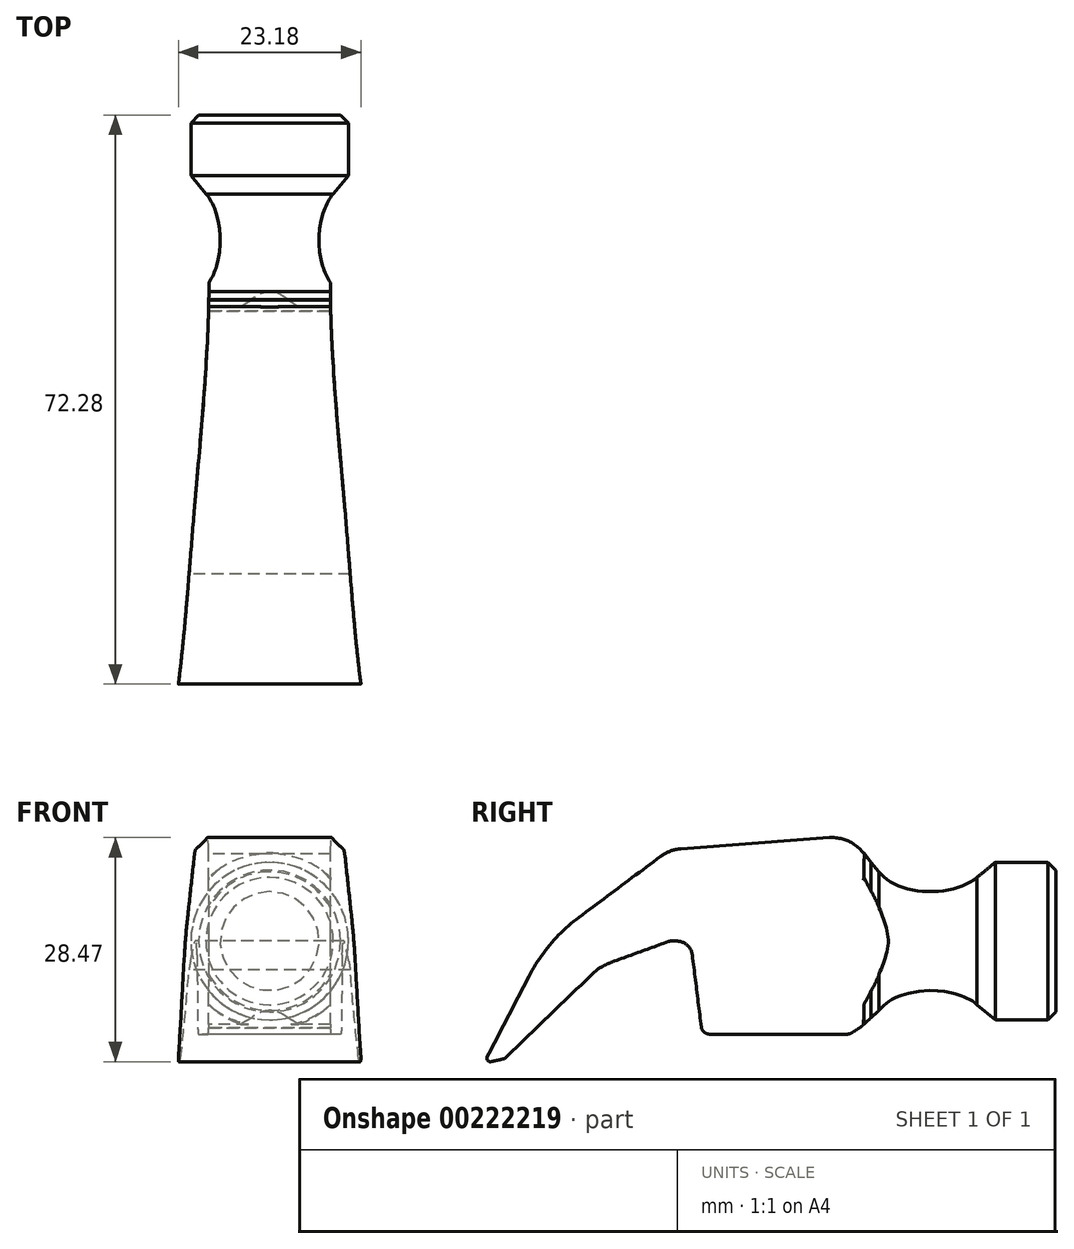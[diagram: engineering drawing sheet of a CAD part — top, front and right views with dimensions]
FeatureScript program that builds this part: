
annotation { "Feature Type Name" : "Feature", "Feature Type Description" : "" }
export const myFeature = defineFeature(function(context is Context, id is Id, definition is map)
    precondition{}
    {
        {
            var Q0;
            Q0=qCreatedBy(makeId("Front.planeOp"),FACE);
            var sketch = newSketch(context, id + "F0", { "sketchPlane" : qUnion([Q0])});
            skCircle(sketch, "E0", {"center": v(0, 0) * mm, "radius": 10 * mm});
            skSolve(sketch);
        }
        {
            var Q0;
            Q0=makeQuery(id+"F0.imprint","IMPRINT",FACE,{"disambiguationData":[TD([[makeQuery(id+"F0.imprint","IMPRINT",EDGE,{"derivedFrom":sQuery(id+"F0.wireOp",EDGE,"E0")}),1.0]])]});
            extrude(context, id + "F1", {"entities" : qUnion([Q0]), "depth" : 25 * mm});
        }
        {
            var Q0;
            Q0=qCreatedBy(makeId("Right.planeOp"),FACE);
            var sketch = newSketch(context, id + "F2", { "sketchPlane" : qUnion([Q0])});
            skEllipse(sketch, "E1", {"center": v(-15.9, 10.31) * mm, "majorRadius": 7.06 * mm, "minorRadius": 4.03 * mm, "majorAxis": v(1, 0)});
            skLineSegment(sketch, "E2", {"start": v(-7.3, 10.31) * mm, "end": v(-10, 8.09) * mm});
            skPoint(sketch, "E2.startSnap0", {"position": v(-8.84, 10.31) * mm});
            skLineSegment(sketch, "E3", {"start": v(-7.3, 10.31) * mm, "end": v(-8.84, 10.31) * mm});
            skSolve(sketch);
        }
        {
            var Q0;
            Q0=makeQuery(id+"F1.opExtrude","CAP_EDGE",EDGE,{"disambiguationData":[OSD([sQuery(id+"F0.wireOp",EDGE,"E0")])],"isStart":false});
            chamfer(context, id + "F3", {"entities" : qUnion([Q0]), "width" : 1 * mm, "tangentPropagation" : true});
        }
        {
            var Q0;
            Q0=makeQuery(id+"F1.opExtrude","CAP_EDGE",EDGE,{"disambiguationData":[OSD([sQuery(id+"F0.wireOp",EDGE,"E0")])],"isStart":true});
            chamfer(context, id + "F4", {"entities" : qUnion([Q0]), "width" : 1 * mm, "tangentPropagation" : true});
        }
        {
            var Q0;
            Q0 = qSketchRegion(id + "F2", true);
            var Q1;
            Q1=makeQuery(id+"F1.opExtrude","SWEPT_FACE",FACE,{"disambiguationData":[OSD([sQuery(id+"F0.wireOp",EDGE,"E0")])]});
            revolve(context, id + "F5", {"operationType" : NewBodyOperationType.REMOVE, "entities" : qUnion([Q0]), "axis" : qUnion([Q1]), "revolveType" : RevolveType.FULL, "oppositeDirection" : true});
        }
        {
            var Q0;
            Q0=qCreatedBy(makeId("Right.planeOp"),FACE);
            var sketch = newSketch(context, id + "F6", { "sketchPlane" : qUnion([Q0])});
            skLineSegment(sketch, "E4", {"start": v(-24.33, 11.06) * mm, "end": v(-24.54, 11.32) * mm});
            skLineSegment(sketch, "E5", {"start": v(-28.78, 13.14) * mm, "end": v(-47.6, 11.73) * mm});
            skLineSegment(sketch, "E6", {"start": v(-50.22, 10.75) * mm, "end": v(-60.56, 3.02) * mm});
            skLineSegment(sketch, "E7", {"start": v(-66.93, -4.48) * mm, "end": v(-72.23, -14.7) * mm});
            skLineSegment(sketch, "E8", {"start": v(-71.76, -15.32) * mm, "end": v(-70.06, -14.95) * mm});
            skLineSegment(sketch, "E9", {"start": v(-70.06, -14.95) * mm, "end": v(-58.3, -3.63) * mm});
            skLineSegment(sketch, "E10", {"start": v(-56.06, -2.55) * mm, "end": v(-49.22, -0.06) * mm});
            skLineSegment(sketch, "E11", {"start": v(-48.88, 0) * mm, "end": v(-48.16, 0) * mm});
            skLineSegment(sketch, "E12", {"start": v(-46.18, -1.75) * mm, "end": v(-45.03, -10.95) * mm});
            skLineSegment(sketch, "E13", {"start": v(-44.04, -11.82) * mm, "end": v(-26.48, -11.82) * mm});
            skLineSegment(sketch, "E14", {"start": v(-25.94, -11.66) * mm, "end": v(-24.86, -10.97) * mm});
            skLineSegment(sketch, "E15", {"start": v(-24.86, -10.97) * mm, "end": v(-24.33, 11.06) * mm});
            skPoint(sketch, "E16.visualSharp", {"position": v(-26.19, 13.33) * mm});
            skArc(sketch, "E16.filletArc", {"start": v(-24.54, 11.32) * mm, "mid": v(-26.44, 12.75) * mm, "end": v(-28.78, 13.14) * mm});
            skPoint(sketch, "E17.visualSharp", {"position": v(-49.05, 11.62) * mm});
            skArc(sketch, "E17.filletArc", {"start": v(-47.6, 11.73) * mm, "mid": v(-48.98, 11.42) * mm, "end": v(-50.22, 10.75) * mm});
            skPoint(sketch, "E18.visualSharp", {"position": v(-64.6, 0) * mm});
            skArc(sketch, "E18.filletArc", {"start": v(-60.56, 3.02) * mm, "mid": v(-64.17, -0.37) * mm, "end": v(-66.93, -4.48) * mm});
            skPoint(sketch, "E19.visualSharp", {"position": v(-44.92, -11.82) * mm});
            skArc(sketch, "E19.filletArc", {"start": v(-45.03, -10.95) * mm, "mid": v(-44.7, -11.57) * mm, "end": v(-44.04, -11.82) * mm});
            skPoint(sketch, "E20.visualSharp", {"position": v(-26.19, -11.82) * mm});
            skArc(sketch, "E20.filletArc", {"start": v(-26.48, -11.82) * mm, "mid": v(-26.2, -11.78) * mm, "end": v(-25.94, -11.66) * mm});
            skPoint(sketch, "E21.visualSharp", {"position": v(-46.4, 0) * mm});
            skArc(sketch, "E21.filletArc", {"start": v(-46.18, -1.75) * mm, "mid": v(-46.84, -0.5) * mm, "end": v(-48.16, 0) * mm});
            skPoint(sketch, "E22.visualSharp", {"position": v(-49.05, 0) * mm});
            skArc(sketch, "E22.filletArc", {"start": v(-48.88, 0) * mm, "mid": v(-49.05, -0.02) * mm, "end": v(-49.22, -0.06) * mm});
            skPoint(sketch, "E23.visualSharp", {"position": v(-57.84, -3.2) * mm});
            skPoint(sketch, "E24.visualSharp", {"position": v(-72.65, -15.5) * mm});
            skArc(sketch, "E24.filletArc", {"start": v(-72.23, -14.7) * mm, "mid": v(-72.2, -15.16) * mm, "end": v(-71.76, -15.32) * mm});
            skPoint(sketch, "E25.visualSharp", {"position": v(-70.06, -14.95) * mm});
            skArc(sketch, "E25.filletArc", {"start": v(-70.06, -14.95) * mm, "mid": v(-70.06, -14.95) * mm, "end": v(-70.06, -14.95) * mm});
            skPoint(sketch, "E26", {"position": v(-57.3, -4.06) * mm});
            skPoint(sketch, "E27", {"position": v(-57.23, -4.15) * mm});
            skPoint(sketch, "E28", {"position": v(-57.49, -3.07) * mm});
            skPoint(sketch, "E29", {"position": v(-58.09, -3.43) * mm});
            skPoint(sketch, "E30", {"position": v(-57.64, -3.12) * mm});
            skPoint(sketch, "E31", {"position": v(-58, -3.34) * mm});
            skLineSegment(sketch, "E32", {"start": v(-58.22, -3.59) * mm, "end": v(-58.3, -3.63) * mm});
            skPoint(sketch, "E33.visualSharp", {"position": v(-57.2, -2.96) * mm});
            skArc(sketch, "E33.filletArc", {"start": v(-56.06, -2.55) * mm, "mid": v(-57.17, -3.01) * mm, "end": v(-58.22, -3.59) * mm});
            skSolve(sketch);
        }
        {
            var Q0;
            Q0=makeQuery(id+"F6.imprint","IMPRINT",FACE,{"disambiguationData":[TD([[makeQuery(id+"F6.imprint","IMPRINT",EDGE,{"derivedFrom":sQuery(id+"F6.wireOp",EDGE,"E4")}),1.0]])]});
            extrude(context, id + "F7", {"entities" : qUnion([Q0]), "operationType" : NewBodyOperationType.ADD, "endBound" : BoundingType.SYMMETRIC, "depth" : 25 * mm});
        }
        {
            var Q0;
            Q0=qCreatedBy(makeId("Right.planeOp"),FACE);
            var sketch = newSketch(context, id + "F8", { "sketchPlane" : qUnion([Q0])});
            skLineSegment(sketch, "E34", {"start": v(-24.37, 11.07) * mm, "end": v(-22.32, 8.66) * mm});
            skLineSegment(sketch, "E35", {"start": v(-22.32, 8.66) * mm, "end": v(-22.32, 11.39) * mm});
            skLineSegment(sketch, "E36", {"start": v(-22.32, 11.39) * mm, "end": v(-24.37, 11.07) * mm});
            skSolve(sketch);
        }
        {
            var Q0;
            Q0 = qSketchRegion(id + "F8", true);
            var Q1;
            Q1=makeQuery(id+"F5.boolean.opBoolean","INTERSECT",EDGE,{"derivedFrom":[makeQuery(id+"F1.opExtrude","SWEPT_FACE",FACE,{"disambiguationData":[OSD([sQuery(id+"F0.wireOp",EDGE,"E0")])]}),makeQuery(id+"F5.opRevolve","SWEPT_FACE",FACE,{"disambiguationData":[OSD([sQuery(id+"F2.wireOp",EDGE,"E1")])]})]});
            revolve(context, id + "F9", {"operationType" : NewBodyOperationType.REMOVE, "entities" : qUnion([Q0]), "axis" : qUnion([Q1]), "revolveType" : RevolveType.FULL, "oppositeDirection" : true});
        }
        {
            var Q0;
            Q0=qCreatedBy(makeId("Right.planeOp"),FACE);
            var sketch = newSketch(context, id + "F10", { "sketchPlane" : qUnion([Q0])});
            skLineSegment(sketch, "E37", {"start": v(-24.37, 11.18) * mm, "end": v(-23.49, 10) * mm});
            skLineSegment(sketch, "E38", {"start": v(-23.49, 10) * mm, "end": v(-24.87, 8.52) * mm});
            skLineSegment(sketch, "E39", {"start": v(-24.87, 8.52) * mm, "end": v(-24.37, 11.18) * mm});
            skSolve(sketch);
        }
        {
            var Q0;
            Q0 = qSketchRegion(id + "F10", true);
            var Q1;
            {var subQ0=sQuery(id+"F0.wireOp",EDGE,"E0");Q1=makeQuery(id+"F3.opChamfer","BLEND_EDGE",EDGE,{"blendedFrom":[makeQuery(id+"F1.opExtrude","CAP_EDGE",EDGE,{"disambiguationData":[OSD([subQ0])],"isStart":false}),makeQuery(id+"F1.opExtrude","SWEPT_FACE",FACE,{"disambiguationData":[OSD([subQ0])]})],"blendedInto":[makeQuery(id+"F1.opExtrude","SWEPT_FACE",FACE,{"disambiguationData":[OSD([subQ0])]})]});}
            revolve(context, id + "F11", {"operationType" : NewBodyOperationType.ADD, "entities" : qUnion([Q0]), "axis" : qUnion([Q1]), "revolveType" : RevolveType.FULL});
        }
        {
            var Q0;
            Q0=qCreatedBy(makeId("Top.planeOp"),FACE);
            var sketch = newSketch(context, id + "F12", { "sketchPlane" : qUnion([Q0])});
            skFitSpline(sketch, "E40", {"points": [v(11.8, -73.72) * mm, v(9.6, -50.62) * mm, v(7.71, -20.6) * mm], "startDerivative": vector(-6.27, 43.8) * mm, "endDerivative": vector(0.34, 53.9) * mm});
            skLineSegment(sketch, "E41", {"start": v(7.71, -20.6) * mm, "end": v(17.16, -20.6) * mm});
            skLineSegment(sketch, "E42", {"start": v(17.16, -20.6) * mm, "end": v(17.16, -73.7) * mm});
            skLineSegment(sketch, "E43", {"start": v(17.16, -73.7) * mm, "end": v(11.8, -73.72) * mm});
            skLineSegment(sketch, "E44.MirrorCS", {"start": v(-17.16, -20.6) * mm, "end": v(-17.16, -73.7) * mm});
            skFitSpline(sketch, "E45.MirrorCS", {"points": [v(-11.8, -73.72) * mm, v(-9.6, -50.62) * mm, v(-7.71, -20.6) * mm], "startDerivative": vector(6.27, 43.8) * mm, "endDerivative": vector(-0.34, 53.9) * mm});
            skLineSegment(sketch, "E46.MirrorCS", {"start": v(-17.16, -73.7) * mm, "end": v(-11.8, -73.72) * mm});
            skLineSegment(sketch, "E47.MirrorCS", {"start": v(-7.71, -20.6) * mm, "end": v(-17.16, -20.6) * mm});
            skSolve(sketch);
        }
        {
            var Q0;
            Q0=qCreatedBy(makeId("Right.planeOp"),FACE);
            var sketch = newSketch(context, id + "F13", { "sketchPlane" : qUnion([Q0])});
            skLineSegment(sketch, "E48", {"start": v(-24.36, -7.77) * mm, "end": v(-24.99, -10.98) * mm});
            skLineSegment(sketch, "E49", {"start": v(-24.99, -10.98) * mm, "end": v(-24.99, -5.64) * mm});
            skLineSegment(sketch, "E50", {"start": v(-24.99, -5.64) * mm, "end": v(-24.62, -3.76) * mm});
            skLineSegment(sketch, "E51", {"start": v(-24.62, -3.76) * mm, "end": v(-24.36, -7.77) * mm});
            skLineSegment(sketch, "E52", {"start": v(-24.99, -10.98) * mm, "end": v(-24.43, -11.1) * mm});
            skLineSegment(sketch, "E53", {"start": v(-24.43, -11.1) * mm, "end": v(-24.36, -7.77) * mm});
            skSolve(sketch);
        }
        {
            var Q0;
            Q0=qCreatedBy(makeId("Right.planeOp"),FACE);
            var sketch = newSketch(context, id + "F14", { "sketchPlane" : qUnion([Q0])});
            skLineSegment(sketch, "E54", {"start": v(-22.44, -8.8) * mm, "end": v(-24.92, -11.05) * mm});
            skLineSegment(sketch, "E55", {"start": v(-24.92, -11.05) * mm, "end": v(-24.42, -11.9) * mm});
            skLineSegment(sketch, "E56", {"start": v(-24.42, -11.9) * mm, "end": v(-22.44, -8.8) * mm});
            skSolve(sketch);
        }
        {
            var Q0;
            Q0 = qSketchRegion(id + "F13", true);
            extrude(context, id + "F15", {"entities" : qUnion([Q0]), "operationType" : NewBodyOperationType.ADD, "endBound" : BoundingType.SYMMETRIC, "depth" : 25 * mm});
        }
        {
            var Q0;
            Q0 = qSketchRegion(id + "F12", true);
            extrude(context, id + "F16", {"entities" : qUnion([Q0]), "operationType" : NewBodyOperationType.REMOVE, "endBound" : BoundingType.SYMMETRIC, "oppositeDirection" : true, "depth" : 50 * mm});
        }
        {
            var Q0;
            Q0=makeQuery(id+"F14.imprint","IMPRINT",FACE,{"disambiguationData":[TD([[makeQuery(id+"F14.imprint","IMPRINT",EDGE,{"derivedFrom":sQuery(id+"F14.wireOp",EDGE,"E54")}),1.0]])]});
            extrude(context, id + "F17", {"entities" : qUnion([Q0]), "operationType" : NewBodyOperationType.REMOVE, "endBound" : BoundingType.SYMMETRIC, "oppositeDirection" : true, "depth" : 25 * mm});
        }
    });
